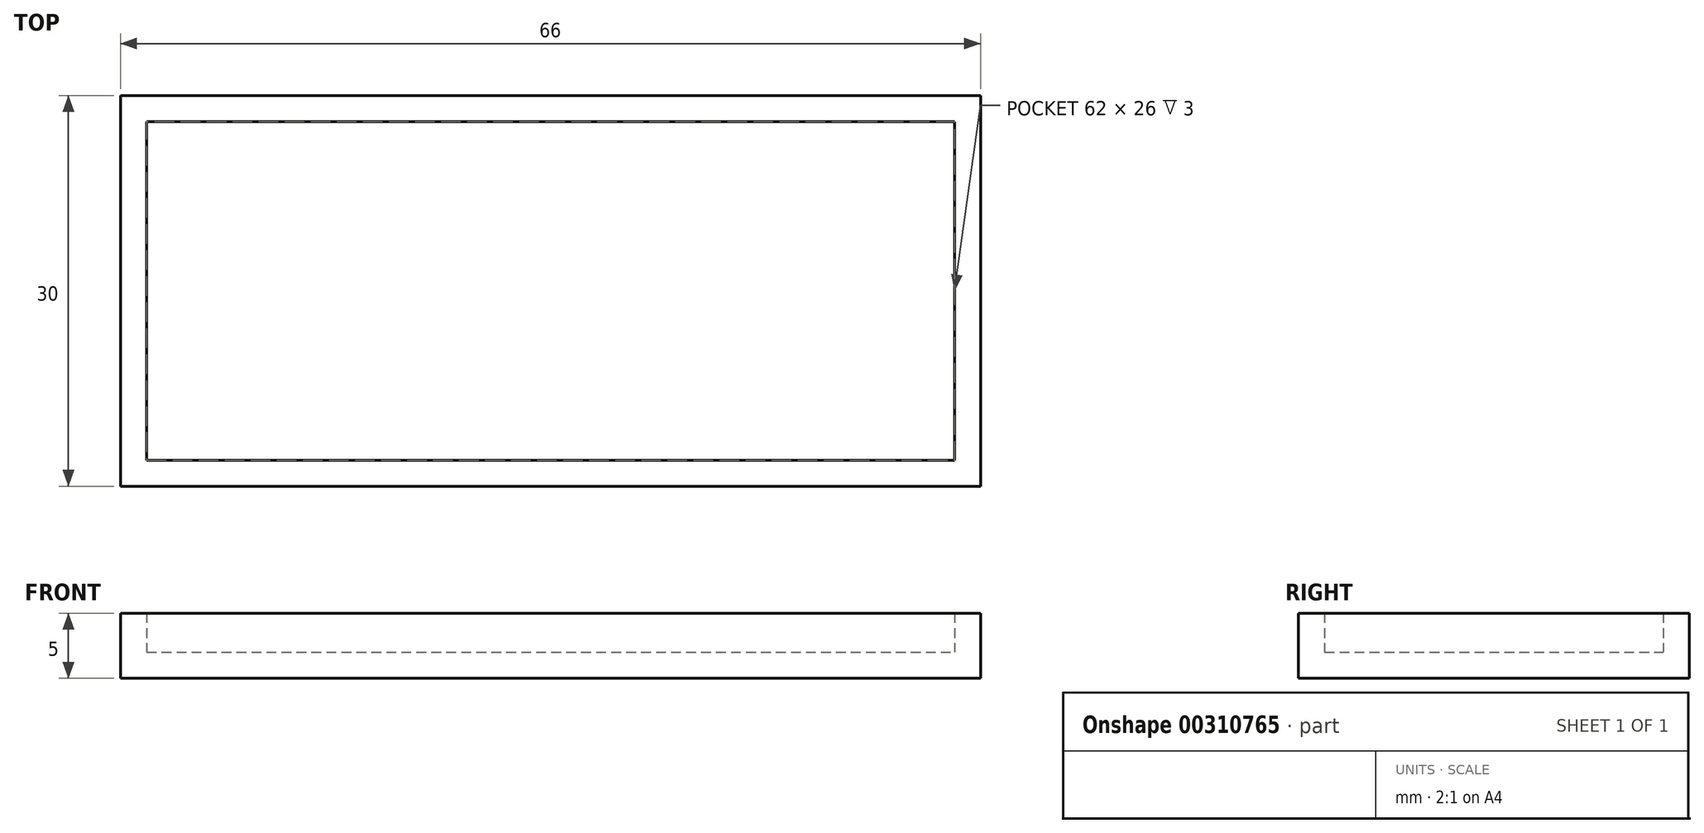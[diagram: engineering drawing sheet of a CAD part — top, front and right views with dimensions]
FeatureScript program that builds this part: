
annotation { "Feature Type Name" : "Feature", "Feature Type Description" : "" }
export const myFeature = defineFeature(function(context is Context, id is Id, definition is map)
    precondition{}
    {
        {
            var Q0;
            Q0=qCreatedBy(makeId("Top.planeOp"),FACE);
            var sketch = newSketch(context, id + "F0", { "sketchPlane" : qUnion([Q0])});
            skLineSegment(sketch, "E0", {"start": v(-33, 15) * mm, "end": v(0, 15) * mm});
            skLineSegment(sketch, "E1", {"start": v(0, 15) * mm, "end": v(33, 15) * mm});
            skLineSegment(sketch, "E2", {"start": v(33, 15) * mm, "end": v(33, 0) * mm});
            skLineSegment(sketch, "E3", {"start": v(33, 0) * mm, "end": v(33, -15) * mm});
            skLineSegment(sketch, "E4", {"start": v(33, -15) * mm, "end": v(0, -15) * mm});
            skLineSegment(sketch, "E5", {"start": v(0, -15) * mm, "end": v(-33, -15) * mm});
            skLineSegment(sketch, "E6", {"start": v(-33, -15) * mm, "end": v(-33, 0) * mm});
            skLineSegment(sketch, "E7", {"start": v(-33, 0) * mm, "end": v(-33, 15) * mm});
            skSolve(sketch);
        }
        {
            var Q0;
            Q0=makeQuery(id+"F0.imprint","IMPRINT",FACE,{"disambiguationData":[TD([[makeQuery(id+"F0.imprint","IMPRINT",EDGE,{"derivedFrom":sQuery(id+"F0.wireOp",EDGE,"E0")}),-1.0]])]});
            extrude(context, id + "F1", {"entities" : qUnion([Q0]), "depth" : 5 * mm});
        }
        {
            var Q0;
            Q0=makeQuery(id+"F1.opExtrude","CAP_FACE",FACE,{"disambiguationData":[OSD([sQuery(id+"F0.wireOp",EDGE,"E0"),sQuery(id+"F0.wireOp",EDGE,"E1"),sQuery(id+"F0.wireOp",EDGE,"E2"),sQuery(id+"F0.wireOp",EDGE,"E3"),sQuery(id+"F0.wireOp",EDGE,"E4"),sQuery(id+"F0.wireOp",EDGE,"E5"),sQuery(id+"F0.wireOp",EDGE,"E6"),sQuery(id+"F0.wireOp",EDGE,"E7")])],"isStart":false});
            shell(context, id + "F2", {"entities" : qUnion([Q0]), "thickness" : 2 * mm});
        }
    });
